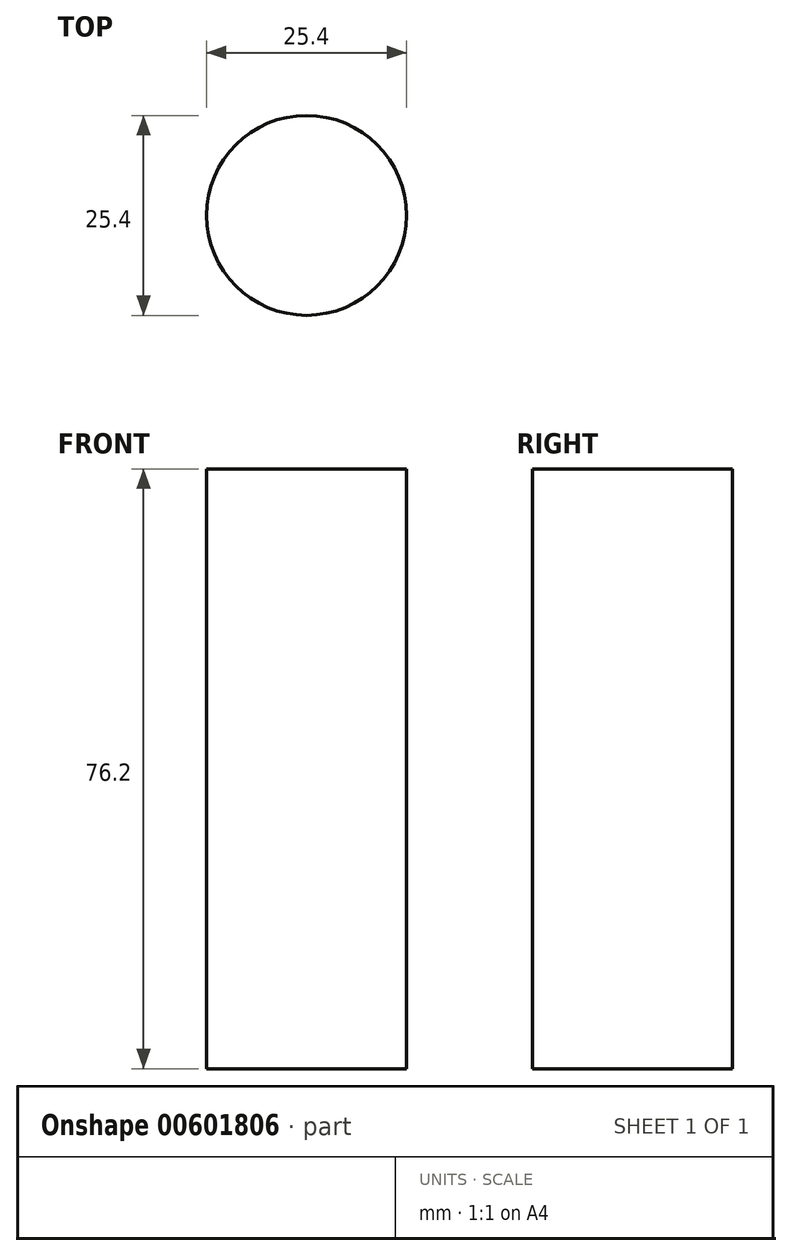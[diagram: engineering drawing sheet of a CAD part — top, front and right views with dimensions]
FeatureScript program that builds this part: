
annotation { "Feature Type Name" : "Feature", "Feature Type Description" : "" }
export const myFeature = defineFeature(function(context is Context, id is Id, definition is map)
    precondition{}
    {
        {
            var Q0;
            Q0=qCreatedBy(makeId("Front.planeOp"),FACE);
            var sketch = newSketch(context, id + "F0", { "sketchPlane" : qUnion([Q0])});
            skPoint(sketch, "E0.start.orphan", {"position": v(0, 76.2) * mm});
            skLineSegment(sketch, "E1", {"start": v(0, 0) * mm, "end": v(0, 76.2) * mm});
            skLineSegment(sketch, "E2", {"start": v(0, 76.2) * mm, "end": v(12.7, 76.2) * mm});
            skLineSegment(sketch, "E3", {"start": v(12.7, 76.2) * mm, "end": v(12.7, 0) * mm});
            skLineSegment(sketch, "E4", {"start": v(12.7, 0) * mm, "end": v(0, 0) * mm});
            skLineSegment(sketch, "E5", {"start": v(6.35, 0) * mm, "end": v(6.35, -15) * mm});
            skLineSegment(sketch, "E6", {"start": v(6.35, -15) * mm, "end": v(0, -15) * mm});
            skLineSegment(sketch, "E7", {"start": v(0, -15) * mm, "end": v(0, 0) * mm});
            skLineSegment(sketch, "E8", {"start": v(6.35, 0) * mm, "end": v(0, 0) * mm});
            skSolve(sketch);
        }
        {
            var Q0;
            Q0=makeQuery(id+"F0.imprint","IMPRINT",FACE,{"disambiguationData":[TD([[makeQuery(id+"F0.imprint","IMPRINT",EDGE,{"derivedFrom":sQuery(id+"F0.wireOp",EDGE,"E1")}),-1.0]])]});
            var Q1;
            Q1=sQuery(id+"F0.wireOp",EDGE,"E3");
            revolve(context, id + "F1", {"entities" : qUnion([Q0]), "axis" : qUnion([Q1]), "revolveType" : RevolveType.FULL});
        }
    });
